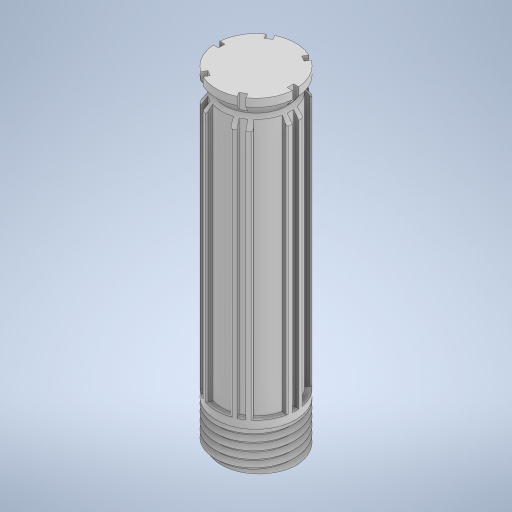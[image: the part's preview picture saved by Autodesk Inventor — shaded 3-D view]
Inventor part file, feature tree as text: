
AUTODESK INVENTOR PART (.ipt)
format: ipt  version: 2024 (Build 280153000, 153)  size: 538,624 bytes
history: native  units: mm
features: sketch x7, extrude x5, pattern_circular x2, fillet x2, other x1, revolve x1
ambient origin geometry x8: Origin, YZ Plane, XZ Plane, XY Plane, X Axis, Y Axis, Z Axis, Center Point
bodies: Volumenkörper1 (feature_tree)
feature tree (18):
  extrude  "Extrusion1"  Depth=61.7mm TaperAngle=0.0deg
  other  "Spirale1"
  extrude  "Extrusion9"  Depth=3.5mm
  revolve  "Umdrehung1"
  extrude  "Extrusion6"  Depth=2.0mm
  pattern_circular  "Runde Anordnung1"  Count=4  [1 undecoded]
  extrude  "Extrusion7"  Depth=7.5mm TaperAngle=360.0deg
  pattern_circular  "Runde Anordnung2"  [2 undecoded]
  fillet  "Rundung4"  Radius=27.0mm
  fillet  "Rundung5"  Radius=60.0mm
  extrude  "Extrusion8"  Depth=0.29mm
  sketch  "Skizze1"  dims[d0=15.0mm d1=61.7mm d2=0.0mm]
  sketch  "Skizze6"  dims[d20=1.5mm d21=3.5mm]
  sketch  "Skizze8"  dims[d22=2.0mm d23=2.0mm]
  sketch  "Skizze9"  dims[d24=90.0deg]
  sketch  "Skizze12"  dims[d32=1.0mm]
  sketch  "Skizze13"  dims[d33=0.6mm]
  sketch  "Skizze14"  dims[d34=0.6mm d35=40.0mm d36=21.85mm d37=0.0mm d38=0.0mm d39=60.0mm d40=360.0deg d42=1.0mm d43=27.0mm d44=21.85mm d45=0.0mm d46=0.0mm d47=60.0mm d48=360.0deg d50=0.29mm d51=1.0mm d52=0.29mm d53=13.0mm d54=15.0mm d56=1.4mm d58=1.4mm d59=9.85mm d60=10.0mm d61=0.0mm d62=90.0deg d63=90.0deg d64=0.0mm d65=0.0mm d66=1.5mm d67=0.0mm d68=15.0mm d69=52.8mm d70=0.0mm d71=60.0deg d72=0.2mm d73=7.5mm d74=15.0mm d55=0.0mm]
note: 3 required parameter values undecoded (feature->parameter linkage not recoverable at this tier; creation-order binding heuristic only, values carry confidence <= 0.55)
